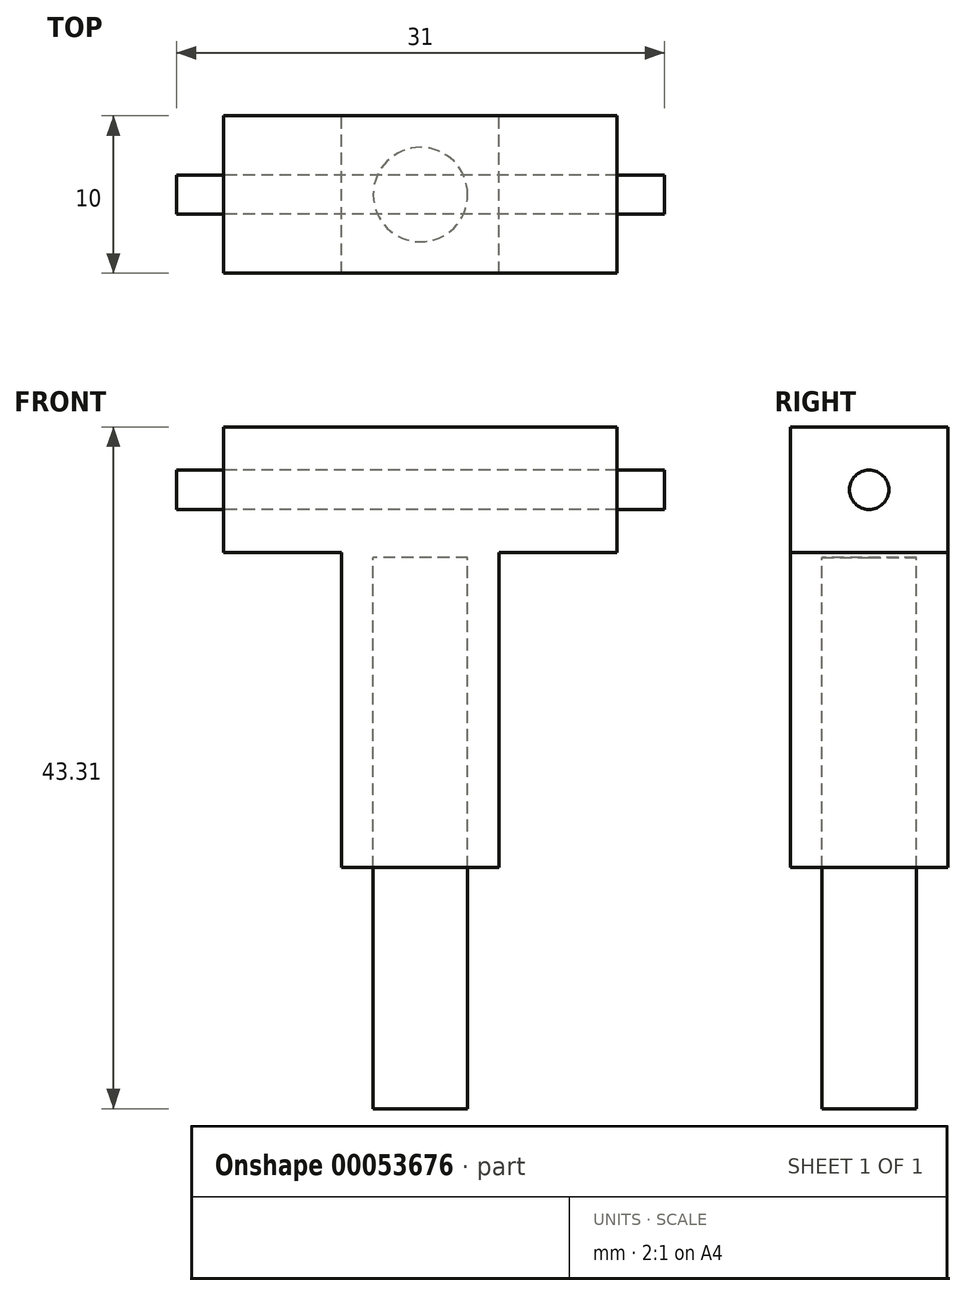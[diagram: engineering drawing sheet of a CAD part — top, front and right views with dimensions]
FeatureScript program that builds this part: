
annotation { "Feature Type Name" : "Feature", "Feature Type Description" : "" }
export const myFeature = defineFeature(function(context is Context, id is Id, definition is map)
    precondition{}
    {
        {
            var Q0;
            Q0=qCreatedBy(makeId("Front.planeOp"),FACE);
            var sketch = newSketch(context, id + "F0", { "sketchPlane" : qUnion([Q0])});
            skLineSegment(sketch, "E0", {"start": v(0, 23) * mm, "end": v(0, -45) * mm, "construction": true});
            skLineSegment(sketch, "E1.bottom", {"start": v(0, -4.3) * mm, "end": v(3, -4.3) * mm});
            skLineSegment(sketch, "E1.top", {"start": v(0, -39.3) * mm, "end": v(3, -39.3) * mm});
            skLineSegment(sketch, "E1.left", {"start": v(0, -4.3) * mm, "end": v(0, -39.3) * mm});
            skLineSegment(sketch, "E1.right", {"start": v(3, -4.3) * mm, "end": v(3, -39.3) * mm});
            skSolve(sketch);
        }
        {
            var Q0;
            Q0 = qSketchRegion(id + "F0", true);
            var Q1;
            Q1=sQuery(id+"F0.wireOp",EDGE,"E0");
            revolve(context, id + "F1", {"entities" : qUnion([Q0]), "axis" : qUnion([Q1]), "revolveType" : RevolveType.FULL});
        }
        {
            var Q0;
            Q0=qCreatedBy(makeId("Front.planeOp"),FACE);
            var sketch = newSketch(context, id + "F2", { "sketchPlane" : qUnion([Q0])});
            skLineSegment(sketch, "E2", {"start": v(-34.05, 0) * mm, "end": v(29.76, 0) * mm, "construction": true});
            skLineSegment(sketch, "E3.bottom", {"start": v(-15.5, 0) * mm, "end": v(15.5, 0) * mm});
            skLineSegment(sketch, "E3.top", {"start": v(-15.5, 1.25) * mm, "end": v(15.5, 1.25) * mm});
            skLineSegment(sketch, "E3.left", {"start": v(-15.5, 0) * mm, "end": v(-15.5, 1.25) * mm});
            skLineSegment(sketch, "E3.right", {"start": v(15.5, 0) * mm, "end": v(15.5, 1.25) * mm});
            skSolve(sketch);
        }
        {
            var Q0;
            Q0 = qSketchRegion(id + "F2", true);
            var Q1;
            Q1=sQuery(id+"F2.wireOp",EDGE,"E2");
            revolve(context, id + "F3", {"entities" : qUnion([Q0]), "axis" : qUnion([Q1]), "revolveType" : RevolveType.FULL});
        }
        {
            var Q0;
            Q0=qCreatedBy(makeId("Front.planeOp"),FACE);
            var sketch = newSketch(context, id + "F4", { "sketchPlane" : qUnion([Q0])});
            skLineSegment(sketch, "E4.rect.bottom", {"start": v(12.5, 4) * mm, "end": v(-12.5, 4) * mm});
            skLineSegment(sketch, "E4.rect.top", {"start": v(12.5, -4) * mm, "end": v(-12.5, -4) * mm});
            skLineSegment(sketch, "E4.rect.left", {"start": v(12.5, 4) * mm, "end": v(12.5, -4) * mm});
            skLineSegment(sketch, "E4.rect.right", {"start": v(-12.5, 4) * mm, "end": v(-12.5, -4) * mm});
            skPoint(sketch, "E4.rect.middle", {"position": v(0, 0) * mm});
            skLineSegment(sketch, "E5.rect.bottom", {"start": v(5, -4) * mm, "end": v(-5, -4) * mm});
            skLineSegment(sketch, "E5.rect.top", {"start": v(5, -24) * mm, "end": v(-5, -24) * mm});
            skLineSegment(sketch, "E5.rect.left", {"start": v(5, -4) * mm, "end": v(5, -24) * mm});
            skLineSegment(sketch, "E5.rect.right", {"start": v(-5, -4) * mm, "end": v(-5, -24) * mm});
            skPoint(sketch, "E5.rect.middle", {"position": v(0, -14) * mm});
            skSolve(sketch);
        }
        {
            var Q0;
            Q0 = qSketchRegion(id + "F4", true);
            extrude(context, id + "F5", {"entities" : qUnion([Q0]), "endBound" : BoundingType.SYMMETRIC, "depth" : 10 * mm});
        }
    });
